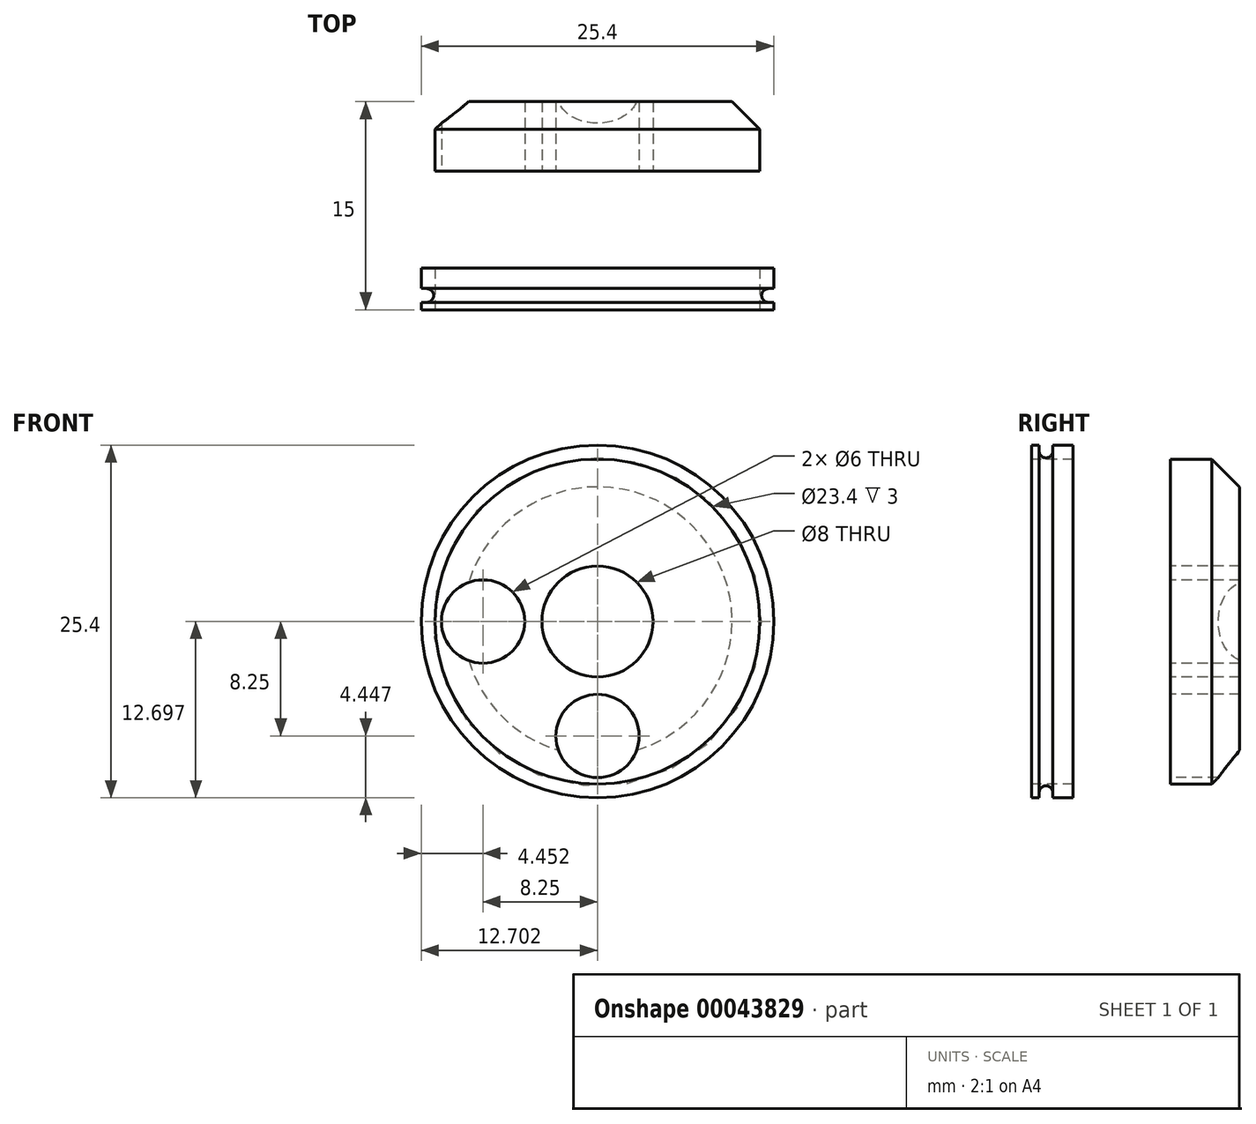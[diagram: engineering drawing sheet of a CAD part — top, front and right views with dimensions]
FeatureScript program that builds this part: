
annotation { "Feature Type Name" : "Feature", "Feature Type Description" : "" }
export const myFeature = defineFeature(function(context is Context, id is Id, definition is map)
    precondition{}
    {
        {
            var Q0;
            Q0=qCreatedBy(makeId("Front.planeOp"),FACE);
            var sketch = newSketch(context, id + "F0", { "sketchPlane" : qUnion([Q0])});
            skCircle(sketch, "E0", {"center": v(0, 0.03) * mm, "radius": 4 * mm});
            skLineSegment(sketch, "E1", {"start": v(0, 0.03) * mm, "end": v(25.08, 0.03) * mm, "construction": true});
            skLineSegment(sketch, "E2", {"start": v(0, 0.03) * mm, "end": v(0, -21.89) * mm, "construction": true});
            skCircle(sketch, "E3", {"center": v(8.24, 0.03) * mm, "radius": 3 * mm});
            skCircle(sketch, "E4.MirrorC", {"center": v(-8.26, 0.03) * mm, "radius": 3 * mm});
            skCircle(sketch, "E5", {"center": v(0, 0.03) * mm, "radius": 12.7 * mm});
            skCircle(sketch, "E6", {"center": v(0, 0.03) * mm, "radius": 8.25 * mm, "construction": true});
            skCircle(sketch, "E7", {"center": v(0, 8.28) * mm, "radius": 3 * mm});
            skCircle(sketch, "E8.MirrorC", {"center": v(0, -8.22) * mm, "radius": 3 * mm});
            skCircle(sketch, "E9.0", {"center": v(0, 0.03) * mm, "radius": 11.7 * mm});
            skSolve(sketch);
        }
        {
            var Q0;
            Q0=makeQuery(id+"F0.imprint","IMPRINT",FACE,{"disambiguationData":[TD([[makeQuery(id+"F0.imprint","IMPRINT",EDGE,{"derivedFrom":sQuery(id+"F0.wireOp",EDGE,"E0")}),-1.0]])]});
            var Q1;
            Q1=makeQuery(id+"F0.imprint","IMPRINT",FACE,{"disambiguationData":[TD([[makeQuery(id+"F0.imprint","IMPRINT",EDGE,{"derivedFrom":sQuery(id+"F0.wireOp",EDGE,"E5")}),1.0]])]});
            var Q2;
            Q2=makeQuery(id+"F0.imprint","IMPRINT",FACE,{"disambiguationData":[TD([[makeQuery(id+"F0.imprint","IMPRINT",EDGE,{"derivedFrom":sQuery(id+"F0.wireOp",EDGE,"E4.MirrorC")}),-1.0]])]});
            var Q3;
            Q3=makeQuery(id+"F0.imprint","IMPRINT",FACE,{"disambiguationData":[TD([[makeQuery(id+"F0.imprint","IMPRINT",EDGE,{"derivedFrom":sQuery(id+"F0.wireOp",EDGE,"E8.MirrorC")}),-1.0]])]});
            var Q4;
            Q4=makeQuery(id+"F0.imprint","IMPRINT",FACE,{"disambiguationData":[TD([[makeQuery(id+"F0.imprint","IMPRINT",EDGE,{"derivedFrom":sQuery(id+"F0.wireOp",EDGE,"E3")}),1.0]])]});
            var Q5;
            Q5=makeQuery(id+"F0.imprint","IMPRINT",FACE,{"disambiguationData":[TD([[makeQuery(id+"F0.imprint","IMPRINT",EDGE,{"derivedFrom":sQuery(id+"F0.wireOp",EDGE,"E7")}),1.0]])]});
            extrude(context, id + "F1", {"entities" : qUnion([Q0, Q1, Q2, Q3, Q4, Q5]), "oppositeDirection" : true, "depth" : 3 * mm});
        }
        {
            var Q0;
            Q0=makeQuery(id+"F0.imprint","IMPRINT",FACE,{"disambiguationData":[TD([[makeQuery(id+"F0.imprint","IMPRINT",EDGE,{"derivedFrom":sQuery(id+"F0.wireOp",EDGE,"E0")}),-1.0]])]});
            var Q1;
            Q1=makeQuery(id+"F0.imprint","IMPRINT",FACE,{"disambiguationData":[TD([[makeQuery(id+"F0.imprint","IMPRINT",EDGE,{"derivedFrom":sQuery(id+"F0.wireOp",EDGE,"E4.MirrorC")}),-1.0]])]});
            var Q2;
            Q2=makeQuery(id+"F0.imprint","IMPRINT",FACE,{"disambiguationData":[TD([[makeQuery(id+"F0.imprint","IMPRINT",EDGE,{"derivedFrom":sQuery(id+"F0.wireOp",EDGE,"E7")}),1.0]])]});
            var Q3;
            Q3=makeQuery(id+"F0.imprint","IMPRINT",FACE,{"disambiguationData":[TD([[makeQuery(id+"F0.imprint","IMPRINT",EDGE,{"derivedFrom":sQuery(id+"F0.wireOp",EDGE,"E3")}),1.0]])]});
            var Q4;
            Q4=makeQuery(id+"F0.imprint","IMPRINT",FACE,{"disambiguationData":[TD([[makeQuery(id+"F0.imprint","IMPRINT",EDGE,{"derivedFrom":sQuery(id+"F0.wireOp",EDGE,"E8.MirrorC")}),-1.0]])]});
            extrude(context, id + "F2", {"entities" : qUnion([Q0, Q1, Q2, Q3, Q4]), "operationType" : NewBodyOperationType.ADD, "oppositeDirection" : true, "depth" : 15 * mm});
        }
        {
            var Q0;
            Q0=makeQuery(id+"F0.imprint","IMPRINT",FACE,{"disambiguationData":[TD([[makeQuery(id+"F0.imprint","IMPRINT",EDGE,{"derivedFrom":sQuery(id+"F0.wireOp",EDGE,"E4.MirrorC")}),-1.0]])]});
            var Q1;
            Q1=makeQuery(id+"F0.imprint","IMPRINT",FACE,{"disambiguationData":[TD([[makeQuery(id+"F0.imprint","IMPRINT",EDGE,{"derivedFrom":sQuery(id+"F0.wireOp",EDGE,"E7")}),1.0]])]});
            var Q2;
            Q2=makeQuery(id+"F0.imprint","IMPRINT",FACE,{"disambiguationData":[TD([[makeQuery(id+"F0.imprint","IMPRINT",EDGE,{"derivedFrom":sQuery(id+"F0.wireOp",EDGE,"E3")}),1.0]])]});
            var Q3;
            Q3=makeQuery(id+"F0.imprint","IMPRINT",FACE,{"disambiguationData":[TD([[makeQuery(id+"F0.imprint","IMPRINT",EDGE,{"derivedFrom":sQuery(id+"F0.wireOp",EDGE,"E8.MirrorC")}),-1.0]])]});
            extrude(context, id + "F3", {"entities" : qUnion([Q0, Q1, Q2, Q3]), "operationType" : NewBodyOperationType.REMOVE, "oppositeDirection" : true, "depth" : 10 * mm});
        }
        {
            var Q0;
            Q0=qCreatedBy(makeId("Top.planeOp"),FACE);
            var sketch = newSketch(context, id + "F4", { "sketchPlane" : qUnion([Q0])});
            skLineSegment(sketch, "E10", {"start": v(-12.72, 3.34) * mm, "end": v(-12.72, 1.54) * mm});
            skLineSegment(sketch, "E11", {"start": v(0, 0) * mm, "end": v(0, 2.56) * mm});
            skLineSegment(sketch, "E12.0", {"start": v(-12.32, 3.34) * mm, "end": v(-12.32, 1.54) * mm});
            skArc(sketch, "E13", {"start": v(-12.32, 0.54) * mm, "mid": v(-11.82, 1.04) * mm, "end": v(-12.32, 1.54) * mm});
            skLineSegment(sketch, "E14", {"start": v(-12.32, 1.54) * mm, "end": v(-13.74, 1.54) * mm});
            skLineSegment(sketch, "E15", {"start": v(-12.32, 0.54) * mm, "end": v(-13.74, 0.54) * mm});
            skLineSegment(sketch, "E16", {"start": v(-13.74, 1.54) * mm, "end": v(-13.74, 0.54) * mm});
            skLineSegment(sketch, "E17.trimOffspring", {"start": v(-12.72, 1.34) * mm, "end": v(-12.72, 0.74) * mm});
            skLineSegment(sketch, "E18.trimOffspring", {"start": v(-12.32, 0.54) * mm, "end": v(-12.32, -2.6) * mm});
            skSolve(sketch);
        }
        {
            var Q0;
            Q0=qSketchRegion(id+"F4",true);
            var Q1;
            Q1=sQuery(id+"F4.wireOp",EDGE,"E11");
            revolve(context, id + "F5", {"operationType" : NewBodyOperationType.REMOVE, "entities" : qUnion([Q0]), "axis" : qUnion([Q1]), "revolveType" : RevolveType.FULL, "oppositeDirection" : true});
        }
        {
            var Q0;
            Q0=qSketchRegion(id+"F4",true);
            var Q1;
            Q1=sQuery(id+"F4.wireOp",EDGE,"E11");
            revolve(context, id + "F6", {"operationType" : NewBodyOperationType.REMOVE, "entities" : qUnion([Q0]), "axis" : qUnion([Q1]), "revolveType" : RevolveType.FULL});
        }
        {
            var Q0;
            Q0=makeQuery(id+"F2.opExtrude","CAP_EDGE",EDGE,{"disambiguationData":[OSD([sQuery(id+"F0.wireOp",EDGE,"E9.0")])],"isStart":false});
            chamfer(context, id + "F7", {"entities" : qUnion([Q0]), "width" : 2 * mm, "tangentPropagation" : true});
        }
    });
